# Revit family: Faucet_Touchless-Wall_Mount-Lavatory-KOHLER-Parallel-K-30737T
name_source: partatom
category: Plumbing Fixtures
units: mm (PartAtom-declared; Revit-internal decimal feet)

## family parameters
Cut with Voids When Loaded = No
Host = Face
OmniClass Number = 23.31.11.00
OmniClass Title = Faucets
Part Type = Normal
Room Calculation Point = No
Round Connector Dimension = Use Diameter
Shared = No

## types (5) — shared parameters
ADA Compliant = No
Assembly Code = D2010
CW Connection = Yes
Cold Water Inlet = Cold Water Inlet
Date Modified = 09/13/2023
Default Elevation = 36"
Description = Single Control Wall Mount Touchless Lavatory Faucet A
Drain Included = Yes
Faucet Hole Spacing = 0"
Flow Rate = 2 GPM
HW Connection = Yes
Handle Clearance = 2 1/4"
Height = 4 1/16"
Hot Water Inlet = Hot Water Inlet
Length = 7 1/4"
Manufacturer = Kohler Co.
Master Format 2014 = 22 41 39
Master Format 2014 Name = Residential Faucets, Supplies, and Trim
Material = Premium Metal Construction
Pressure = 40.00 psi
Product Name = Parallel
Spout Reach = 7 1/4"
URL = http://www.kohler.com.cn
Vent Connection = No
Waste Connection = No
Waste Water Outlet = Waste Water Outlet
WaterSense Certified = No
Width = 7 9/16"

## per-type parameters (varying)
| type | Finish | Model | Secondary Faucet | Type |
| CP-Polished Chrome | Kohler-Metal-CP-Polished_Chrome | K-30737T-4-CP | Plastic-Pantone-423C | 1 |
| AF-Vibrant French Gold | Kohler-Metal-AF-Vibrant_French_Gold | K-30737T-4-AF | Plastic-Pantone-1234U | 2 |
| BN-Vibrant Brushed Nickel | Kohler-Metal-BN-Vibrant_Brushed_Nickel | K-30737T-4-BN | Plastic-Pantone-423C | 3 |
| RGD-Polished Rose Gold | Kohler-Metal-RGD-Polished_Rose_Gold | K-30737T-4-RGD | Plastic-Pantone-1234U | 4 |
| BL-Matte Black | Kohler-Metal-BL-Matte_Black | K-30737T-4-BL | Plastic-Pantone-433C | 5 |

## geometry (parser evidence)
native form markers: Sweep x5
no freeform markers — native parametric forms only
